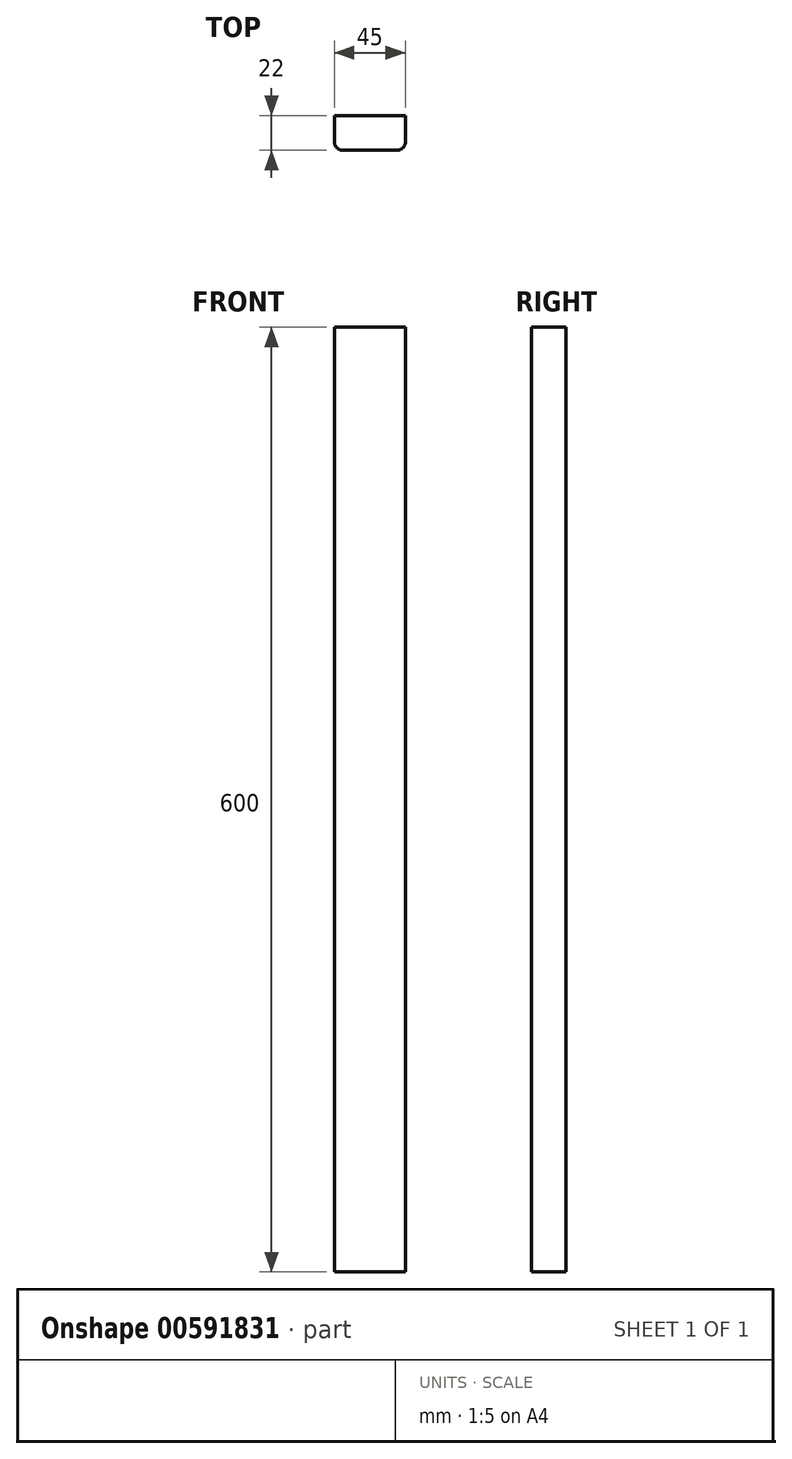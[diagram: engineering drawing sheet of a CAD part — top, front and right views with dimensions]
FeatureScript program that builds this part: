
annotation { "Feature Type Name" : "Feature", "Feature Type Description" : "" }
export const myFeature = defineFeature(function(context is Context, id is Id, definition is map)
    precondition{}
    {
        {
            var Q0;
            Q0=qCreatedBy(makeId("Top.planeOp"),FACE);
            var sketch = newSketch(context, id + "F0", { "sketchPlane" : qUnion([Q0])});
            skLineSegment(sketch, "E0.bottom", {"start": v(5, 0) * mm, "end": v(40, 0) * mm});
            skLineSegment(sketch, "E0.top", {"start": v(0, 22) * mm, "end": v(45, 22) * mm});
            skLineSegment(sketch, "E0.left", {"start": v(0, 5) * mm, "end": v(0, 22) * mm});
            skLineSegment(sketch, "E0.right", {"start": v(45, 5) * mm, "end": v(45, 22) * mm});
            skPoint(sketch, "E1.visualSharp", {"position": v(0, 0) * mm});
            skArc(sketch, "E1.filletArc", {"start": v(0, 5) * mm, "mid": v(1.46, 1.46) * mm, "end": v(5, 0) * mm});
            skPoint(sketch, "E2.visualSharp", {"position": v(45, 0) * mm});
            skArc(sketch, "E2.filletArc", {"start": v(40, 0) * mm, "mid": v(43.54, 1.46) * mm, "end": v(45, 5) * mm});
            skSolve(sketch);
        }
        {
            var Q0;
            Q0=makeQuery(id+"F0.imprint","IMPRINT",FACE,{"disambiguationData":[TD([[makeQuery(id+"F0.imprint","IMPRINT",EDGE,{"derivedFrom":sQuery(id+"F0.wireOp",EDGE,"E0.bottom")}),1.0]])]});
            extrude(context, id + "F1", {"entities" : qUnion([Q0]), "depth" : 600 * mm, "offsetDistance" : 25 * mm});
        }
    });
